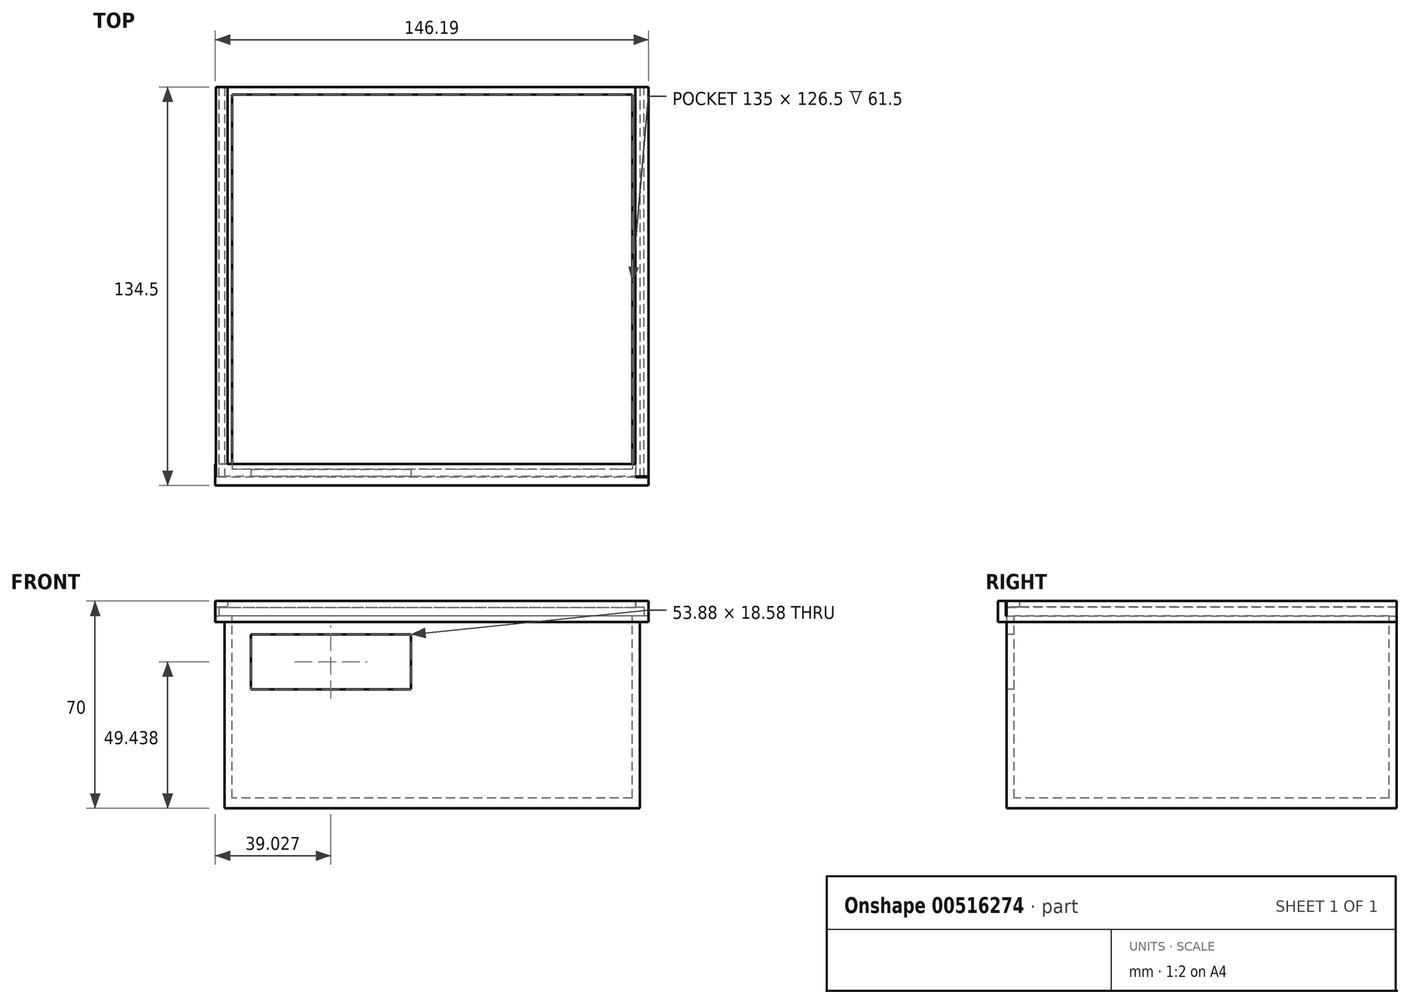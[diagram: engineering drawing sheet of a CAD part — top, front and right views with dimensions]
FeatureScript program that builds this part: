
annotation { "Feature Type Name" : "Feature", "Feature Type Description" : "" }
export const myFeature = defineFeature(function(context is Context, id is Id, definition is map)
    precondition{}
    {
        {
            var Q0;
            Q0=qCreatedBy(makeId("Top.planeOp"),FACE);
            var sketch = newSketch(context, id + "F0", { "sketchPlane" : qUnion([Q0])});
            skLineSegment(sketch, "E0.bottom", {"start": v(70, 65) * mm, "end": v(-70, 65) * mm});
            skLineSegment(sketch, "E0.top", {"start": v(70, -65) * mm, "end": v(-70, -65) * mm});
            skLineSegment(sketch, "E0.left", {"start": v(70, 65) * mm, "end": v(70, -65) * mm});
            skLineSegment(sketch, "E0.right", {"start": v(-70, 65) * mm, "end": v(-70, -65) * mm});
            skPoint(sketch, "E0.middle", {"position": v(0, 0) * mm});
            skSolve(sketch);
        }
        {
            var Q0;
            Q0=makeQuery(id+"F0.imprint","IMPRINT",FACE,{"disambiguationData":[TD([[makeQuery(id+"F0.imprint","IMPRINT",EDGE,{"derivedFrom":sQuery(id+"F0.wireOp",EDGE,"E0.bottom")}),1.0]])]});
            extrude(context, id + "F1", {"entities" : qUnion([Q0]), "depth" : 65 * mm, "offsetDistance" : 25 * mm});
        }
        {
            var Q0;
            Q0=makeQuery(id+"F1.opExtrude","CAP_FACE",FACE,{"disambiguationData":[OSD([sQuery(id+"F0.wireOp",EDGE,"E0.bottom"),sQuery(id+"F0.wireOp",EDGE,"E0.top"),sQuery(id+"F0.wireOp",EDGE,"E0.left"),sQuery(id+"F0.wireOp",EDGE,"E0.right")])],"isStart":false});
            var sketch = newSketch(context, id + "F2", { "sketchPlane" : qUnion([Q0])});
            skLineSegment(sketch, "E1.bottom", {"start": v(69, 64) * mm, "end": v(-69, 64) * mm});
            skLineSegment(sketch, "E1.top", {"start": v(69, -64) * mm, "end": v(-69, -64) * mm});
            skLineSegment(sketch, "E1.left", {"start": v(69, 64) * mm, "end": v(69, -64) * mm});
            skLineSegment(sketch, "E1.right", {"start": v(-69, 64) * mm, "end": v(-69, -64) * mm});
            skPoint(sketch, "E1.middle", {"position": v(0, 0) * mm});
            skSolve(sketch);
        }
        {
            var Q0;
            Q0=makeQuery(id+"F2.imprint","IMPRINT",FACE,{"disambiguationData":[TD([[makeQuery(id+"F2.imprint","IMPRINT",EDGE,{"derivedFrom":sQuery(id+"F2.wireOp",EDGE,"E1.bottom")}),1.0]])]});
            extrude(context, id + "F3", {"entities" : qUnion([Q0]), "operationType" : NewBodyOperationType.REMOVE, "oppositeDirection" : true, "depth" : 63 * mm, "offsetDistance" : 25 * mm});
        }
        {
            var Q0;
            Q0=makeQuery(id+"F1.opExtrude","SWEPT_FACE",FACE,{"disambiguationData":[OSD([sQuery(id+"F0.wireOp",EDGE,"E0.top")])]});
            var sketch = newSketch(context, id + "F4", { "sketchPlane" : qUnion([Q0])});
            skLineSegment(sketch, "E2.bottom", {"start": v(-67.2, 65) * mm, "end": v(-7.2, 65) * mm});
            skLineSegment(sketch, "E2.top", {"start": v(-67.2, 45) * mm, "end": v(-7.2, 45) * mm});
            skLineSegment(sketch, "E2.left", {"start": v(-67.2, 65) * mm, "end": v(-67.2, 45) * mm});
            skLineSegment(sketch, "E2.right", {"start": v(-7.2, 65) * mm, "end": v(-7.2, 45) * mm});
            skSolve(sketch);
        }
        {
            var Q0;
            Q0=makeQuery(id+"F4.imprint","IMPRINT",FACE,{"disambiguationData":[TD([[makeQuery(id+"F4.imprint","IMPRINT",EDGE,{"derivedFrom":sQuery(id+"F4.wireOp",EDGE,"E2.bottom")}),1.0]])]});
            extrude(context, id + "F5", {"entities" : qUnion([Q0]), "operationType" : NewBodyOperationType.REMOVE, "oppositeDirection" : true, "depth" : 25 * mm, "offsetDistance" : 25 * mm});
        }
        {
            var Q0;
            Q0=makeQuery(id+"F1.opExtrude","CAP_FACE",FACE,{"disambiguationData":[OSD([sQuery(id+"F0.wireOp",EDGE,"E0.bottom"),sQuery(id+"F0.wireOp",EDGE,"E0.top"),sQuery(id+"F0.wireOp",EDGE,"E0.left"),sQuery(id+"F0.wireOp",EDGE,"E0.right")])],"isStart":false});
            var sketch = newSketch(context, id + "F6", { "sketchPlane" : qUnion([Q0])});
            skLineSegment(sketch, "E3", {"start": v(-70, 65) * mm, "end": v(-69, 64) * mm});
            skSolve(sketch);
        }
        {
            var Q0;
            Q0=makeQuery(id+"F1.opExtrude","SWEPT_FACE",FACE,{"disambiguationData":[OSD([sQuery(id+"F0.wireOp",EDGE,"E0.left")])]});
            var sketch = newSketch(context, id + "F7", { "sketchPlane" : qUnion([Q0])});
            skLineSegment(sketch, "E4.bottom", {"start": v(65, 65) * mm, "end": v(-65, 65) * mm});
            skLineSegment(sketch, "E4.top", {"start": v(65, 62.91) * mm, "end": v(-65, 62.91) * mm});
            skLineSegment(sketch, "E4.left", {"start": v(65, 65) * mm, "end": v(65, 62.91) * mm});
            skLineSegment(sketch, "E4.right", {"start": v(-65, 65) * mm, "end": v(-65, 62.91) * mm});
            skSolve(sketch);
        }
        {
            var Q0;
            Q0 = qSketchRegion(id + "F7", true);
            extrude(context, id + "F8", {"entities" : qUnion([Q0]), "operationType" : NewBodyOperationType.ADD, "depth" : 3 * mm, "offsetDistance" : 25 * mm});
        }
        {
            var Q0;
            Q0=makeQuery(id+"F8.boolean.opBoolean","MERGE",FACE,{"derivedFrom":[makeQuery(id+"F1.opExtrude","CAP_FACE",FACE,{"disambiguationData":[OSD([sQuery(id+"F0.wireOp",EDGE,"E0.bottom"),sQuery(id+"F0.wireOp",EDGE,"E0.top"),sQuery(id+"F0.wireOp",EDGE,"E0.left"),sQuery(id+"F0.wireOp",EDGE,"E0.right")])],"isStart":false}),makeQuery(id+"F8.opExtrude","SWEPT_FACE",FACE,{"disambiguationData":[OSD([sQuery(id+"F7.wireOp",EDGE,"E4.bottom")])]})]});
            var sketch = newSketch(context, id + "F9", { "sketchPlane" : qUnion([Q0])});
            skLineSegment(sketch, "E5.bottom", {"start": v(71.5, 65) * mm, "end": v(73, 65) * mm});
            skLineSegment(sketch, "E5.top", {"start": v(71.5, -65) * mm, "end": v(73, -65) * mm});
            skLineSegment(sketch, "E5.left", {"start": v(71.5, 65) * mm, "end": v(71.5, -65) * mm});
            skLineSegment(sketch, "E5.right", {"start": v(73, 65) * mm, "end": v(73, -65) * mm});
            skSolve(sketch);
        }
        {
            var Q0;
            Q0 = qSketchRegion(id + "F9", true);
            extrude(context, id + "F10", {"entities" : qUnion([Q0]), "operationType" : NewBodyOperationType.ADD, "depth" : 5 * mm, "offsetDistance" : 25 * mm});
        }
        {
            var Q0;
            Q0=makeQuery(id+"F10.opExtrude","SWEPT_FACE",FACE,{"disambiguationData":[OSD([sQuery(id+"F9.wireOp",EDGE,"E5.left")])]});
            var sketch = newSketch(context, id + "F11", { "sketchPlane" : qUnion([Q0])});
            skLineSegment(sketch, "E6.bottom", {"start": v(65, 68) * mm, "end": v(-65, 68) * mm});
            skLineSegment(sketch, "E6.top", {"start": v(65, 66.5) * mm, "end": v(-65, 66.5) * mm});
            skLineSegment(sketch, "E6.left", {"start": v(65, 68) * mm, "end": v(65, 66.5) * mm});
            skLineSegment(sketch, "E6.right", {"start": v(-65, 68) * mm, "end": v(-65, 66.5) * mm});
            skSolve(sketch);
        }
        {
            var Q0;
            Q0=makeQuery(id+"F11.imprint","IMPRINT",FACE,{"disambiguationData":[TD([[makeQuery(id+"F11.imprint","IMPRINT",EDGE,{"derivedFrom":sQuery(id+"F11.wireOp",EDGE,"E6.bottom")}),-1.0]])]});
            extrude(context, id + "F12", {"entities" : qUnion([Q0]), "operationType" : NewBodyOperationType.ADD, "depth" : 3 * mm, "offsetDistance" : 25 * mm});
        }
        {
            var Q0;
            Q0=makeQuery(id+"F1.opExtrude","SWEPT_FACE",FACE,{"disambiguationData":[OSD([sQuery(id+"F0.wireOp",EDGE,"E0.right")])]});
            var sketch = newSketch(context, id + "F13", { "sketchPlane" : qUnion([Q0])});
            skLineSegment(sketch, "E7.bottom", {"start": v(65, 65) * mm, "end": v(-65, 65) * mm});
            skLineSegment(sketch, "E7.top", {"start": v(65, 63) * mm, "end": v(-65, 63) * mm});
            skLineSegment(sketch, "E7.left", {"start": v(65, 65) * mm, "end": v(65, 63) * mm});
            skLineSegment(sketch, "E7.right", {"start": v(-65, 65) * mm, "end": v(-65, 63) * mm});
            skSolve(sketch);
        }
        {
            var Q0;
            Q0=makeQuery(id+"F13.imprint","IMPRINT",FACE,{"disambiguationData":[TD([[makeQuery(id+"F13.imprint","IMPRINT",EDGE,{"derivedFrom":sQuery(id+"F13.wireOp",EDGE,"E7.bottom")}),-1.0]])]});
            extrude(context, id + "F14", {"entities" : qUnion([Q0]), "operationType" : NewBodyOperationType.ADD, "depth" : 3 * mm, "offsetDistance" : 25 * mm});
        }
        {
            var Q0;
            Q0=makeQuery(id+"F14.boolean.opBoolean","MERGE",FACE,{"derivedFrom":[makeQuery(id+"F8.boolean.opBoolean","MERGE",FACE,{"derivedFrom":[makeQuery(id+"F1.opExtrude","CAP_FACE",FACE,{"disambiguationData":[OSD([sQuery(id+"F0.wireOp",EDGE,"E0.bottom"),sQuery(id+"F0.wireOp",EDGE,"E0.top"),sQuery(id+"F0.wireOp",EDGE,"E0.left"),sQuery(id+"F0.wireOp",EDGE,"E0.right")])],"isStart":false}),makeQuery(id+"F8.opExtrude","SWEPT_FACE",FACE,{"disambiguationData":[OSD([sQuery(id+"F7.wireOp",EDGE,"E4.bottom")])]})]}),makeQuery(id+"F14.opExtrude","SWEPT_FACE",FACE,{"disambiguationData":[OSD([sQuery(id+"F13.wireOp",EDGE,"E7.bottom")])]})]});
            var sketch = newSketch(context, id + "F15", { "sketchPlane" : qUnion([Q0])});
            skLineSegment(sketch, "E8.bottom", {"start": v(-73, -65) * mm, "end": v(-72, -65) * mm});
            skLineSegment(sketch, "E8.top", {"start": v(-73, 65) * mm, "end": v(-72, 65) * mm});
            skLineSegment(sketch, "E8.left", {"start": v(-73, -65) * mm, "end": v(-73, 65) * mm});
            skLineSegment(sketch, "E8.right", {"start": v(-72, -65) * mm, "end": v(-72, 65) * mm});
            skSolve(sketch);
        }
        {
            var Q0;
            Q0 = qSketchRegion(id + "F15", true);
            extrude(context, id + "F16", {"entities" : qUnion([Q0]), "operationType" : NewBodyOperationType.ADD, "depth" : 5 * mm, "offsetDistance" : 25 * mm});
        }
        {
            var Q0;
            Q0=makeQuery(id+"F16.opExtrude","SWEPT_FACE",FACE,{"disambiguationData":[OSD([sQuery(id+"F15.wireOp",EDGE,"E8.right")])]});
            var sketch = newSketch(context, id + "F17", { "sketchPlane" : qUnion([Q0])});
            skLineSegment(sketch, "E9.bottom", {"start": v(65, 70) * mm, "end": v(-65, 70) * mm});
            skLineSegment(sketch, "E9.top", {"start": v(65, 68) * mm, "end": v(-65, 68) * mm});
            skLineSegment(sketch, "E9.left", {"start": v(65, 70) * mm, "end": v(65, 68) * mm});
            skLineSegment(sketch, "E9.right", {"start": v(-65, 70) * mm, "end": v(-65, 68) * mm});
            skSolve(sketch);
        }
        {
            var Q0;
            Q0 = qSketchRegion(id + "F17", true);
            extrude(context, id + "F18", {"entities" : qUnion([Q0]), "operationType" : NewBodyOperationType.ADD, "depth" : 3 * mm, "offsetDistance" : 25 * mm});
        }
        {
            var Q0;
            {var subQ0=sQuery(id+"F9.wireOp",EDGE,"E5.top");var subQ1=sQuery(id+"F7.wireOp",EDGE,"E4.right");var subQ2=sQuery(id+"F0.wireOp",EDGE,"E0.top");Q0=makeQuery(id+"F18.boolean.opBoolean","MERGE",FACE,{"derivedFrom":[makeQuery(id+"F16.boolean.opBoolean","MERGE",FACE,{"derivedFrom":[makeQuery(id+"F14.boolean.opBoolean","MERGE",FACE,{"derivedFrom":[makeQuery(id+"F12.boolean.opBoolean","MERGE",FACE,{"derivedFrom":[makeQuery(id+"F10.boolean.opBoolean","MERGE",FACE,{"derivedFrom":[makeQuery(id+"F8.boolean.opBoolean","MERGE",FACE,{"derivedFrom":[makeQuery(id+"F1.opExtrude","SWEPT_FACE",FACE,{"disambiguationData":[OSD([subQ2])]}),makeQuery(id+"F8.opExtrude","SWEPT_FACE",FACE,{"disambiguationData":[OSD([subQ1])]})]}),makeQuery(id+"F10.opExtrude","SWEPT_FACE",FACE,{"disambiguationData":[OSD([subQ0])]})]}),makeQuery(id+"F12.opExtrude","SWEPT_FACE",FACE,{"disambiguationData":[OSD([subQ2,sQuery(id+"F7.wireOp",EDGE,"E4.bottom"),subQ1,subQ0,sQuery(id+"F9.wireOp",EDGE,"E5.left")])]})]}),makeQuery(id+"F14.opExtrude","SWEPT_FACE",FACE,{"disambiguationData":[OSD([sQuery(id+"F13.wireOp",EDGE,"E7.left")])]})]}),makeQuery(id+"F16.opExtrude","SWEPT_FACE",FACE,{"disambiguationData":[OSD([sQuery(id+"F15.wireOp",EDGE,"E8.bottom")])]})]}),makeQuery(id+"F18.opExtrude","SWEPT_FACE",FACE,{"disambiguationData":[OSD([sQuery(id+"F17.wireOp",EDGE,"E9.right")])]})]});}
            extrude(context, id + "F19", {"entities" : qUnion([Q0]), "operationType" : NewBodyOperationType.ADD, "depth" : 1.5 * mm, "offsetDistance" : 25 * mm});
        }
        {
            var Q0;
            Q0=makeQuery(id+"F3.boolean.opBoolean","COPY",FACE,{"derivedFrom":makeQuery(id+"F3.opExtrude","SWEPT_FACE",FACE,{"disambiguationData":[OSD([sQuery(id+"F2.wireOp",EDGE,"E1.bottom")])]})});
            extrude(context, id + "F20", {"entities" : qUnion([Q0]), "operationType" : NewBodyOperationType.ADD, "depth" : 1.5 * mm, "offsetDistance" : 25 * mm});
        }
        {
            var Q0;
            Q0=makeQuery(id+"F3.boolean.opBoolean","COPY",FACE,{"derivedFrom":makeQuery(id+"F3.opExtrude","SWEPT_FACE",FACE,{"disambiguationData":[OSD([sQuery(id+"F2.wireOp",EDGE,"E1.right")])]})});
            extrude(context, id + "F21", {"entities" : qUnion([Q0]), "operationType" : NewBodyOperationType.ADD, "depth" : 1.5 * mm, "offsetDistance" : 25 * mm});
        }
        {
            var Q0;
            Q0=makeQuery(id+"F3.boolean.opBoolean","COPY",FACE,{"derivedFrom":makeQuery(id+"F3.opExtrude","CAP_FACE",FACE,{"disambiguationData":[OSD([sQuery(id+"F2.wireOp",EDGE,"E1.bottom"),sQuery(id+"F2.wireOp",EDGE,"E1.top"),sQuery(id+"F2.wireOp",EDGE,"E1.left"),sQuery(id+"F2.wireOp",EDGE,"E1.right")])],"isStart":false})});
            extrude(context, id + "F22", {"entities" : qUnion([Q0]), "operationType" : NewBodyOperationType.ADD, "depth" : 1.5 * mm, "offsetDistance" : 25 * mm});
        }
        {
            var Q0;
            Q0=makeQuery(id+"F3.boolean.opBoolean","COPY",FACE,{"derivedFrom":makeQuery(id+"F3.opExtrude","SWEPT_FACE",FACE,{"disambiguationData":[OSD([sQuery(id+"F2.wireOp",EDGE,"E1.left")])]})});
            extrude(context, id + "F23", {"entities" : qUnion([Q0]), "operationType" : NewBodyOperationType.ADD, "depth" : 1.5 * mm, "offsetDistance" : 25 * mm});
        }
        {
            var Q0;
            Q0=makeQuery(id+"F19.opExtrude","CAP_FACE",FACE,{"disambiguationData":[OSD([sQuery(id+"F0.wireOp",EDGE,"E0.top"),sQuery(id+"F7.wireOp",EDGE,"E4.bottom"),sQuery(id+"F7.wireOp",EDGE,"E4.right"),sQuery(id+"F9.wireOp",EDGE,"E5.top"),sQuery(id+"F9.wireOp",EDGE,"E5.left"),sQuery(id+"F13.wireOp",EDGE,"E7.left"),sQuery(id+"F15.wireOp",EDGE,"E8.bottom"),sQuery(id+"F17.wireOp",EDGE,"E9.right")])],"isStart":false});
            var sketch = newSketch(context, id + "F24", { "sketchPlane" : qUnion([Q0])});
            skLineSegment(sketch, "E10.bottom", {"start": v(73, 62.91) * mm, "end": v(-7.2, 62.91) * mm});
            skLineSegment(sketch, "E10.top", {"start": v(73, 65) * mm, "end": v(-7.2, 65) * mm});
            skLineSegment(sketch, "E10.left", {"start": v(73, 62.91) * mm, "end": v(73, 65) * mm});
            skLineSegment(sketch, "E10.right", {"start": v(-7.2, 62.91) * mm, "end": v(-7.2, 65) * mm});
            skSolve(sketch);
        }
        {
            var Q0;
            {var subQ7=sQuery(id+"F24.wireOp",EDGE,"E10.left");Q0=makeQuery(id+"F24.imprint","IMPRINT",FACE,{"disambiguationData":[TD([[makeQuery(id+"F24.imprint","IMPRINT",EDGE,{"derivedFrom":subQ7}),-1.0]])]});}
            extrude(context, id + "F25", {"entities" : qUnion([Q0]), "operationType" : NewBodyOperationType.ADD, "depth" : 3 * mm, "offsetDistance" : 25 * mm});
        }
        {
            var Q0;
            {var subQ0=sQuery(id+"F2.wireOp",EDGE,"E1.left");var subQ1=sQuery(id+"F2.wireOp",EDGE,"E1.right");var subQ2=sQuery(id+"F2.wireOp",EDGE,"E1.bottom");var subQ3=sQuery(id+"F13.wireOp",EDGE,"E7.bottom");var subQ4=sQuery(id+"F0.wireOp",EDGE,"E0.top");var subQ5=sQuery(id+"F7.wireOp",EDGE,"E4.bottom");Q0=makeQuery(id+"F25.boolean.opBoolean","MERGE",FACE,{"derivedFrom":[makeQuery(id+"F23.boolean.opBoolean","MERGE",FACE,{"derivedFrom":[makeQuery(id+"F21.boolean.opBoolean","MERGE",FACE,{"derivedFrom":[makeQuery(id+"F20.boolean.opBoolean","MERGE",FACE,{"derivedFrom":[makeQuery(id+"F19.boolean.opBoolean","MERGE",FACE,{"derivedFrom":[makeQuery(id+"F14.boolean.opBoolean","MERGE",FACE,{"derivedFrom":[makeQuery(id+"F8.boolean.opBoolean","MERGE",FACE,{"derivedFrom":[makeQuery(id+"F1.opExtrude","CAP_FACE",FACE,{"disambiguationData":[OSD([sQuery(id+"F0.wireOp",EDGE,"E0.bottom"),subQ4,sQuery(id+"F0.wireOp",EDGE,"E0.left"),sQuery(id+"F0.wireOp",EDGE,"E0.right")])],"isStart":false}),makeQuery(id+"F8.opExtrude","SWEPT_FACE",FACE,{"disambiguationData":[OSD([subQ5])]})]}),makeQuery(id+"F14.opExtrude","SWEPT_FACE",FACE,{"disambiguationData":[OSD([subQ3])]})]}),makeQuery(id+"F19.opExtrude","SWEPT_FACE",FACE,{"disambiguationData":[OSD([subQ4,subQ5,sQuery(id+"F7.wireOp",EDGE,"E4.right")])]}),makeQuery(id+"F19.opExtrude","SWEPT_FACE",FACE,{"disambiguationData":[OSD([subQ4,subQ3,sQuery(id+"F13.wireOp",EDGE,"E7.left")])]})]}),makeQuery(id+"F20.opExtrude","SWEPT_FACE",FACE,{"disambiguationData":[OSD([subQ2]),TDD([makeQuery(id+"F3.boolean.opBoolean","COPY",EDGE,{"derivedFrom":makeQuery(id+"F3.opExtrude","CAP_EDGE",EDGE,{"disambiguationData":[OSD([subQ2])],"isStart":true})})])]})]}),makeQuery(id+"F21.opExtrude","SWEPT_FACE",FACE,{"disambiguationData":[OSD([subQ1]),TDD([makeQuery(id+"F3.boolean.opBoolean","COPY",EDGE,{"derivedFrom":makeQuery(id+"F3.opExtrude","CAP_EDGE",EDGE,{"disambiguationData":[OSD([subQ1])],"isStart":true})})])]})]}),makeQuery(id+"F23.opExtrude","SWEPT_FACE",FACE,{"disambiguationData":[OSD([subQ0]),TDD([makeQuery(id+"F3.boolean.opBoolean","COPY",EDGE,{"derivedFrom":makeQuery(id+"F3.opExtrude","CAP_EDGE",EDGE,{"disambiguationData":[OSD([subQ0])],"isStart":true})})])]})]}),makeQuery(id+"F25.opExtrude","SWEPT_FACE",FACE,{"disambiguationData":[OSD([sQuery(id+"F24.wireOp",EDGE,"E10.top")])]})]});}
            var sketch = newSketch(context, id + "F26", { "sketchPlane" : qUnion([Q0])});
            skLineSegment(sketch, "E11.bottom", {"start": v(73, -69.5) * mm, "end": v(-7.2, -69.5) * mm});
            skLineSegment(sketch, "E11.top", {"start": v(73, -66.75) * mm, "end": v(-7.2, -66.75) * mm});
            skLineSegment(sketch, "E11.left", {"start": v(73, -69.5) * mm, "end": v(73, -66.75) * mm});
            skLineSegment(sketch, "E11.right", {"start": v(-7.2, -69.5) * mm, "end": v(-7.2, -66.75) * mm});
            skSolve(sketch);
        }
        {
            var Q0;
            Q0=makeQuery(id+"F26.imprint","IMPRINT",FACE,{"disambiguationData":[TD([[makeQuery(id+"F26.imprint","IMPRINT",EDGE,{"derivedFrom":sQuery(id+"F26.wireOp",EDGE,"E11.bottom")}),-1.0]])]});
            extrude(context, id + "F27", {"entities" : qUnion([Q0]), "operationType" : NewBodyOperationType.ADD, "depth" : 5 * mm, "offsetDistance" : 25 * mm});
        }
        {
            var Q0;
            Q0=makeQuery(id+"F27.opExtrude","SWEPT_FACE",FACE,{"disambiguationData":[OSD([sQuery(id+"F26.wireOp",EDGE,"E11.top")])]});
            var sketch = newSketch(context, id + "F28", { "sketchPlane" : qUnion([Q0])});
            skLineSegment(sketch, "E12.bottom", {"start": v(7.2, 70) * mm, "end": v(-68.7, 70) * mm});
            skLineSegment(sketch, "E12.top", {"start": v(7.2, 67.85) * mm, "end": v(-68.7, 67.85) * mm});
            skLineSegment(sketch, "E12.left", {"start": v(7.2, 70) * mm, "end": v(7.2, 67.85) * mm});
            skLineSegment(sketch, "E12.right", {"start": v(-68.7, 70) * mm, "end": v(-68.7, 67.85) * mm});
            skSolve(sketch);
        }
        {
            var Q0;
            Q0 = qSketchRegion(id + "F28", true);
            extrude(context, id + "F29", {"entities" : qUnion([Q0]), "operationType" : NewBodyOperationType.ADD, "depth" : 4.5 * mm, "offsetDistance" : 25 * mm});
        }
        {
            var Q0;
            {var subQ1=sQuery(id+"F0.wireOp",EDGE,"E0.top");var subQ2=sQuery(id+"F17.wireOp",EDGE,"E9.right");var subQ6=sQuery(id+"F15.wireOp",EDGE,"E8.bottom");var subQ10=sQuery(id+"F0.wireOp",EDGE,"E0.left");var subQ13=sQuery(id+"F13.wireOp",EDGE,"E7.left");var subQ15=sQuery(id+"F7.wireOp",EDGE,"E4.bottom");var subQ18=sQuery(id+"F7.wireOp",EDGE,"E4.right");Q0=makeQuery(id+"F25.boolean.opBoolean","SPLIT",FACE,{"disambiguationData":[TD([makeQuery(id+"F1.opExtrude","SWEPT_FACE",FACE,{"disambiguationData":[OSD([subQ10])]})])],"derivedFrom":makeQuery(id+"F19.opExtrude","CAP_FACE",FACE,{"disambiguationData":[OSD([subQ1,subQ15,subQ18,sQuery(id+"F9.wireOp",EDGE,"E5.top"),sQuery(id+"F9.wireOp",EDGE,"E5.left"),subQ13,subQ6,subQ2])],"isStart":false})});}
            var sketch = newSketch(context, id + "F30", { "sketchPlane" : qUnion([Q0])});
            skLineSegment(sketch, "E13.bottom", {"start": v(-7.2, 45) * mm, "end": v(-67.09, 45) * mm});
            skLineSegment(sketch, "E13.top", {"start": v(-7.2, 41) * mm, "end": v(-67.09, 41) * mm});
            skLineSegment(sketch, "E13.left", {"start": v(-7.2, 45) * mm, "end": v(-7.2, 41) * mm});
            skLineSegment(sketch, "E13.right", {"start": v(-67.09, 45) * mm, "end": v(-67.09, 41) * mm});
            skSolve(sketch);
        }
        {
            var Q0;
            Q0=makeQuery(id+"F30.imprint","IMPRINT",FACE,{"disambiguationData":[TD([[makeQuery(id+"F30.imprint","IMPRINT",EDGE,{"derivedFrom":sQuery(id+"F30.wireOp",EDGE,"E13.bottom")}),-1.0]])]});
            extrude(context, id + "F31", {"entities" : qUnion([Q0]), "operationType" : NewBodyOperationType.REMOVE, "oppositeDirection" : true, "depth" : 3 * mm, "offsetDistance" : 25 * mm});
        }
        {
            var Q0;
            {var subQ0=sQuery(id+"F4.wireOp",EDGE,"E2.right");Q0=makeQuery(id+"F31.boolean.opBoolean","MERGE",FACE,{"derivedFrom":[makeQuery(id+"F29.boolean.opBoolean","MERGE",FACE,{"derivedFrom":[makeQuery(id+"F27.boolean.opBoolean","MERGE",FACE,{"derivedFrom":[makeQuery(id+"F25.boolean.opBoolean","MERGE",FACE,{"derivedFrom":[makeQuery(id+"F19.boolean.opBoolean","MERGE",FACE,{"derivedFrom":[makeQuery(id+"F5.boolean.opBoolean","COPY",FACE,{"derivedFrom":makeQuery(id+"F5.opExtrude","SWEPT_FACE",FACE,{"disambiguationData":[OSD([subQ0])]})}),makeQuery(id+"F19.opExtrude","SWEPT_FACE",FACE,{"disambiguationData":[OSD([subQ0])]})]}),makeQuery(id+"F25.opExtrude","SWEPT_FACE",FACE,{"disambiguationData":[OSD([sQuery(id+"F24.wireOp",EDGE,"E10.right")])]})]}),makeQuery(id+"F27.opExtrude","SWEPT_FACE",FACE,{"disambiguationData":[OSD([sQuery(id+"F26.wireOp",EDGE,"E11.right")])]})]}),makeQuery(id+"F29.opExtrude","SWEPT_FACE",FACE,{"disambiguationData":[OSD([sQuery(id+"F28.wireOp",EDGE,"E12.left")])]})]}),makeQuery(id+"F31.opExtrude","SWEPT_FACE",FACE,{"disambiguationData":[OSD([sQuery(id+"F30.wireOp",EDGE,"E13.left")])]})]});}
            extrude(context, id + "F32", {"entities" : qUnion([Q0]), "operationType" : NewBodyOperationType.ADD, "depth" : 62 * mm, "offsetDistance" : 25 * mm});
        }
        {
            var Q0;
            {var subQ0=sQuery(id+"F4.wireOp",EDGE,"E2.right");var subQ2=sQuery(id+"F0.wireOp",EDGE,"E0.top");var subQ3=sQuery(id+"F17.wireOp",EDGE,"E9.right");var subQ7=sQuery(id+"F15.wireOp",EDGE,"E8.bottom");var subQ11=sQuery(id+"F0.wireOp",EDGE,"E0.left");var subQ14=sQuery(id+"F13.wireOp",EDGE,"E7.left");var subQ16=sQuery(id+"F7.wireOp",EDGE,"E4.bottom");var subQ18=sQuery(id+"F7.wireOp",EDGE,"E4.right");Q0=makeQuery(id+"F32.boolean.opBoolean","MERGE",FACE,{"derivedFrom":[makeQuery(id+"F25.boolean.opBoolean","SPLIT",FACE,{"disambiguationData":[TD([makeQuery(id+"F1.opExtrude","SWEPT_FACE",FACE,{"disambiguationData":[OSD([subQ11])]})])],"derivedFrom":makeQuery(id+"F19.opExtrude","CAP_FACE",FACE,{"disambiguationData":[OSD([subQ2,subQ16,subQ18,sQuery(id+"F9.wireOp",EDGE,"E5.top"),sQuery(id+"F9.wireOp",EDGE,"E5.left"),subQ14,subQ7,subQ3])],"isStart":false})}),makeQuery(id+"F32.opExtrude","SWEPT_FACE",FACE,{"disambiguationData":[OSD([subQ0,sQuery(id+"F30.wireOp",EDGE,"E13.left")])]})]});}
            var sketch = newSketch(context, id + "F33", { "sketchPlane" : qUnion([Q0])});
            skLineSegment(sketch, "E14.bottom", {"start": v(-7.22, 58.73) * mm, "end": v(-61.1, 58.73) * mm});
            skLineSegment(sketch, "E14.top", {"start": v(-7.22, 40.15) * mm, "end": v(-61.1, 40.15) * mm});
            skLineSegment(sketch, "E14.left", {"start": v(-7.22, 58.73) * mm, "end": v(-7.22, 40.15) * mm});
            skLineSegment(sketch, "E14.right", {"start": v(-61.1, 58.73) * mm, "end": v(-61.1, 40.15) * mm});
            skSolve(sketch);
        }
        {
            var Q0;
            Q0=makeQuery(id+"F33.imprint","IMPRINT",FACE,{"disambiguationData":[TD([[makeQuery(id+"F33.imprint","IMPRINT",EDGE,{"derivedFrom":sQuery(id+"F33.wireOp",EDGE,"E14.bottom")}),1.0]])]});
            extrude(context, id + "F34", {"entities" : qUnion([Q0]), "operationType" : NewBodyOperationType.REMOVE, "oppositeDirection" : true, "depth" : 3 * mm, "offsetDistance" : 25 * mm});
        }
        {
            var Q0;
            Q0=makeQuery(id+"F32.opExtrude","CAP_FACE",FACE,{"disambiguationData":[OSD([sQuery(id+"F4.wireOp",EDGE,"E2.right"),sQuery(id+"F24.wireOp",EDGE,"E10.right"),sQuery(id+"F26.wireOp",EDGE,"E11.right"),sQuery(id+"F28.wireOp",EDGE,"E12.left"),sQuery(id+"F30.wireOp",EDGE,"E13.left")])],"isStart":false});
            extrude(context, id + "F35", {"entities" : qUnion([Q0]), "operationType" : NewBodyOperationType.ADD, "depth" : 4 * mm, "offsetDistance" : 25 * mm});
        }
    });
